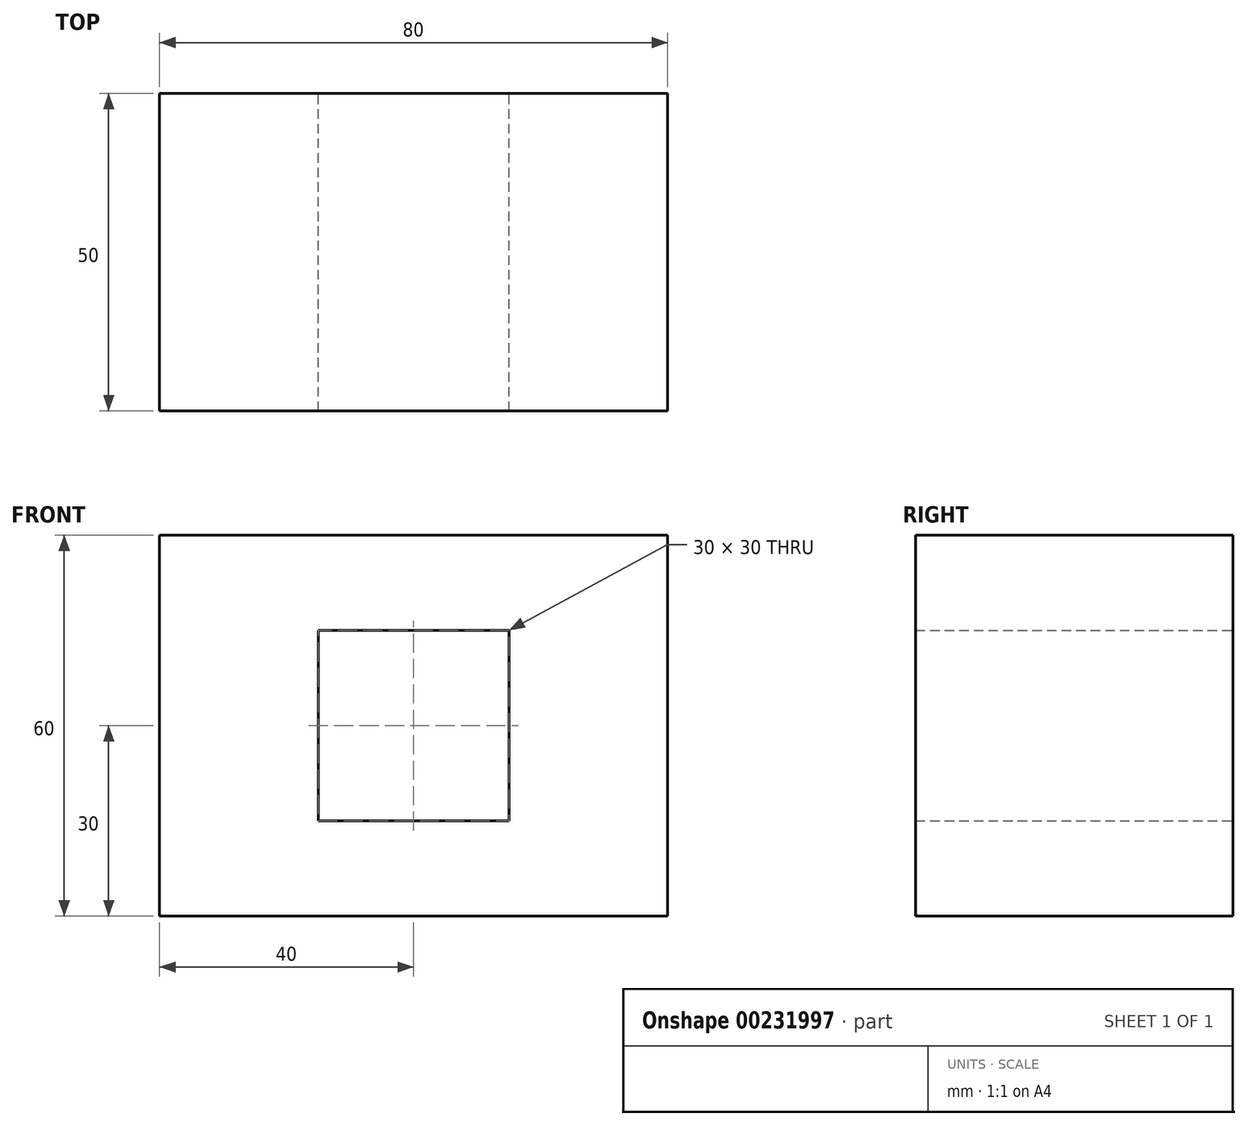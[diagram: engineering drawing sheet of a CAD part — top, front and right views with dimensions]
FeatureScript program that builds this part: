
annotation { "Feature Type Name" : "Feature", "Feature Type Description" : "" }
export const myFeature = defineFeature(function(context is Context, id is Id, definition is map)
    precondition{}
    {
        {
            var Q0;
            Q0=qCreatedBy(makeId("Front.planeOp"),FACE);
            var sketch = newSketch(context, id + "F0", { "sketchPlane" : qUnion([Q0])});
            skLineSegment(sketch, "E0.bottom", {"start": v(0, 0) * mm, "end": v(-80, 0) * mm});
            skLineSegment(sketch, "E0.top", {"start": v(0, 60) * mm, "end": v(-80, 60) * mm});
            skLineSegment(sketch, "E0.left", {"start": v(0, 0) * mm, "end": v(0, 60) * mm});
            skLineSegment(sketch, "E0.right", {"start": v(-80, 0) * mm, "end": v(-80, 60) * mm});
            skLineSegment(sketch, "E1.bottom", {"start": v(-25, 15) * mm, "end": v(-55, 15) * mm});
            skLineSegment(sketch, "E1.top", {"start": v(-25, 45) * mm, "end": v(-55, 45) * mm});
            skLineSegment(sketch, "E1.left", {"start": v(-25, 15) * mm, "end": v(-25, 45) * mm});
            skLineSegment(sketch, "E1.right", {"start": v(-55, 15) * mm, "end": v(-55, 45) * mm});
            skSolve(sketch);
        }
        {
            var Q0;
            Q0=makeQuery(id+"F0.imprint","IMPRINT",FACE,{"disambiguationData":[TD([[makeQuery(id+"F0.imprint","IMPRINT",EDGE,{"derivedFrom":sQuery(id+"F0.wireOp",EDGE,"E0.bottom")}),-1.0]])]});
            extrude(context, id + "F1", {"entities" : qUnion([Q0]), "depth" : 50 * mm});
        }
    });
